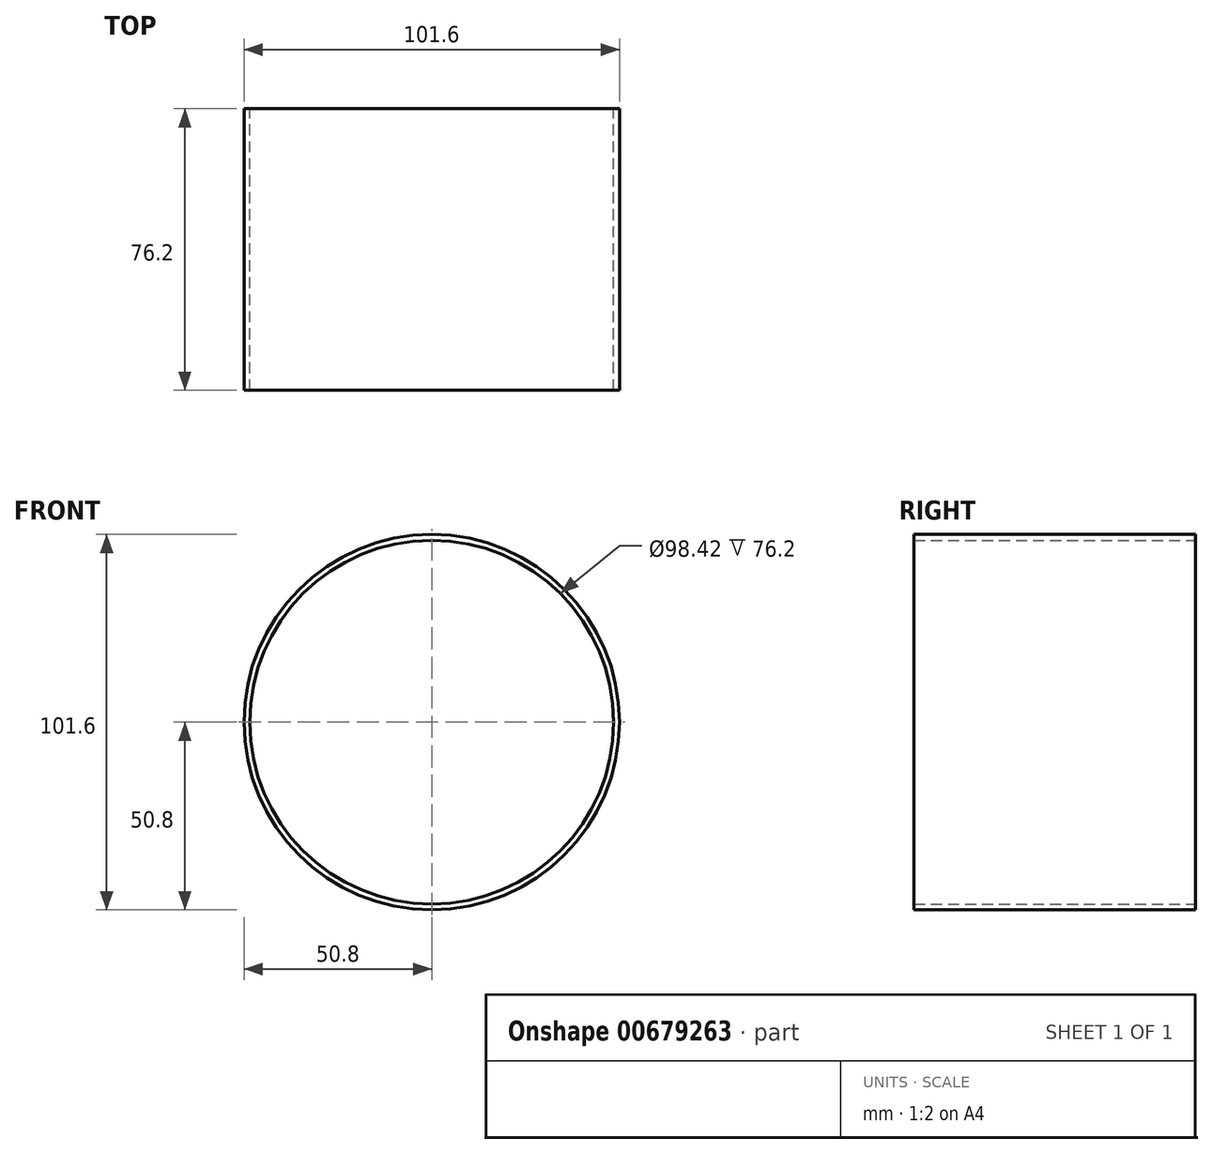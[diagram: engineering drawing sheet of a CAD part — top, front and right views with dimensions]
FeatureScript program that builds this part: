
annotation { "Feature Type Name" : "Feature", "Feature Type Description" : "" }
export const myFeature = defineFeature(function(context is Context, id is Id, definition is map)
    precondition{}
    {
        {
            var Q0;
            Q0=qCreatedBy(makeId("Front.planeOp"),FACE);
            var sketch = newSketch(context, id + "F0", { "sketchPlane" : qUnion([Q0])});
            skCircle(sketch, "E0", {"center": v(0, 0) * mm, "radius": 50.8 * mm});
            skCircle(sketch, "E1.0", {"center": v(0, 0) * mm, "radius": 49.21 * mm});
            skSolve(sketch);
        }
        {
            var Q0;
            Q0=qSketchRegion(id+"F0",true);
            extrude(context, id + "F1", {"entities" : qUnion([Q0]), "depth" : 76.2 * mm, "offsetDistance" : 25.4 * mm});
        }
    });
